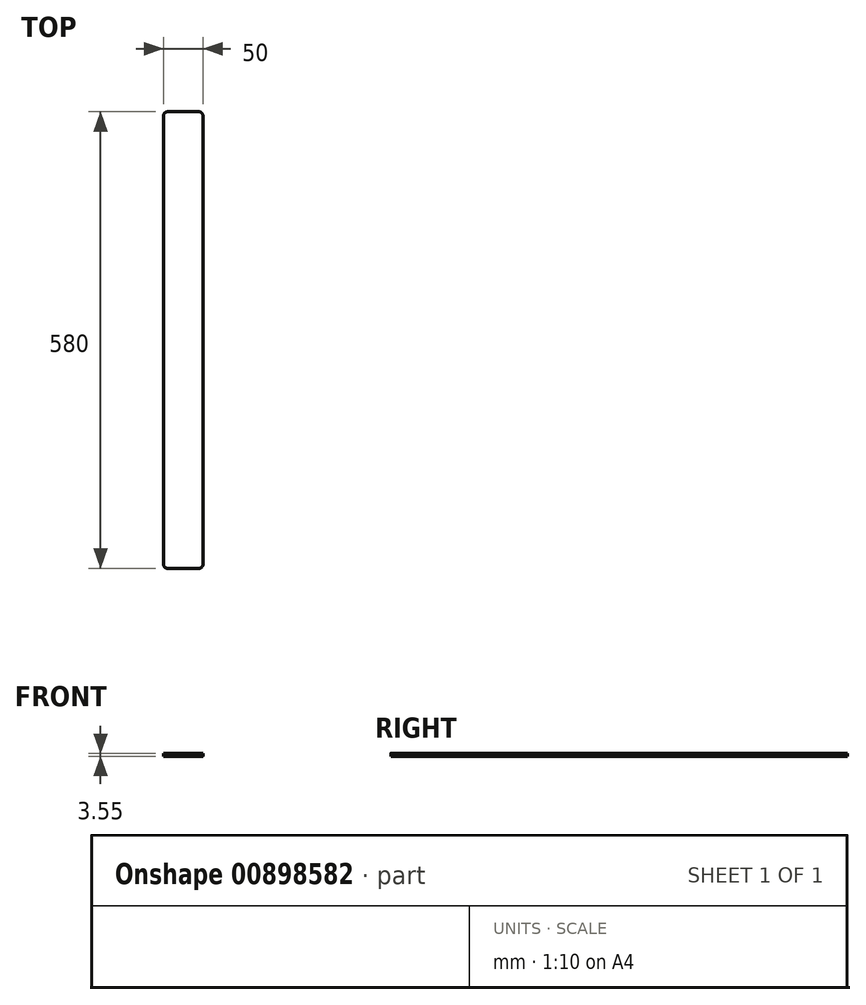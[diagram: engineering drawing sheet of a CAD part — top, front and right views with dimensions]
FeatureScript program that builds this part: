
annotation { "Feature Type Name" : "Feature", "Feature Type Description" : "" }
export const myFeature = defineFeature(function(context is Context, id is Id, definition is map)
    precondition{}
    {
        {
            var Q0;
            Q0=qCreatedBy(makeId("Top.planeOp"),FACE);
            var sketch = newSketch(context, id + "F0", { "sketchPlane" : qUnion([Q0])});
            skLineSegment(sketch, "E0.bottom", {"start": v(25, 290) * mm, "end": v(-25, 290) * mm});
            skLineSegment(sketch, "E0.top", {"start": v(25, -290) * mm, "end": v(-25, -290) * mm});
            skLineSegment(sketch, "E0.left", {"start": v(25, 290) * mm, "end": v(25, -290) * mm});
            skLineSegment(sketch, "E0.right", {"start": v(-25, 290) * mm, "end": v(-25, -290) * mm});
            skPoint(sketch, "E0.middle", {"position": v(0, 0) * mm});
            skSolve(sketch);
        }
        {
            var Q0;
            Q0=makeQuery(id+"F0.imprint","IMPRINT",FACE,{"disambiguationData":[TD([[makeQuery(id+"F0.imprint","IMPRINT",EDGE,{"derivedFrom":sQuery(id+"F0.wireOp",EDGE,"E0.bottom")}),1.0]])]});
            extrude(context, id + "F1", {"entities" : qUnion([Q0]), "depth" : 3.55 * mm, "offsetDistance" : 25 * mm});
        }
        {
            var Q0;
            Q0=makeQuery(id+"F1.opExtrude","SWEPT_EDGE",EDGE,{"disambiguationData":[OSD([sQuery(id+"F0.wireOp",EDGE,"E0.bottom"),sQuery(id+"F0.wireOp",EDGE,"E0.left")])]});
            var Q1;
            Q1=makeQuery(id+"F1.opExtrude","SWEPT_EDGE",EDGE,{"disambiguationData":[OSD([sQuery(id+"F0.wireOp",EDGE,"E0.bottom"),sQuery(id+"F0.wireOp",EDGE,"E0.right")])]});
            var Q2;
            Q2=makeQuery(id+"F1.opExtrude","SWEPT_EDGE",EDGE,{"disambiguationData":[OSD([sQuery(id+"F0.wireOp",EDGE,"E0.top"),sQuery(id+"F0.wireOp",EDGE,"E0.left")])]});
            var Q3;
            Q3=makeQuery(id+"F1.opExtrude","SWEPT_EDGE",EDGE,{"disambiguationData":[OSD([sQuery(id+"F0.wireOp",EDGE,"E0.top"),sQuery(id+"F0.wireOp",EDGE,"E0.right")])]});
            fillet(context, id + "F2", {"entities" : qUnion([Q0, Q1, Q2, Q3]), "radius" : 5 * mm, "tangentPropagation" : true, "allowEdgeOverflow" : false});
        }
    });
